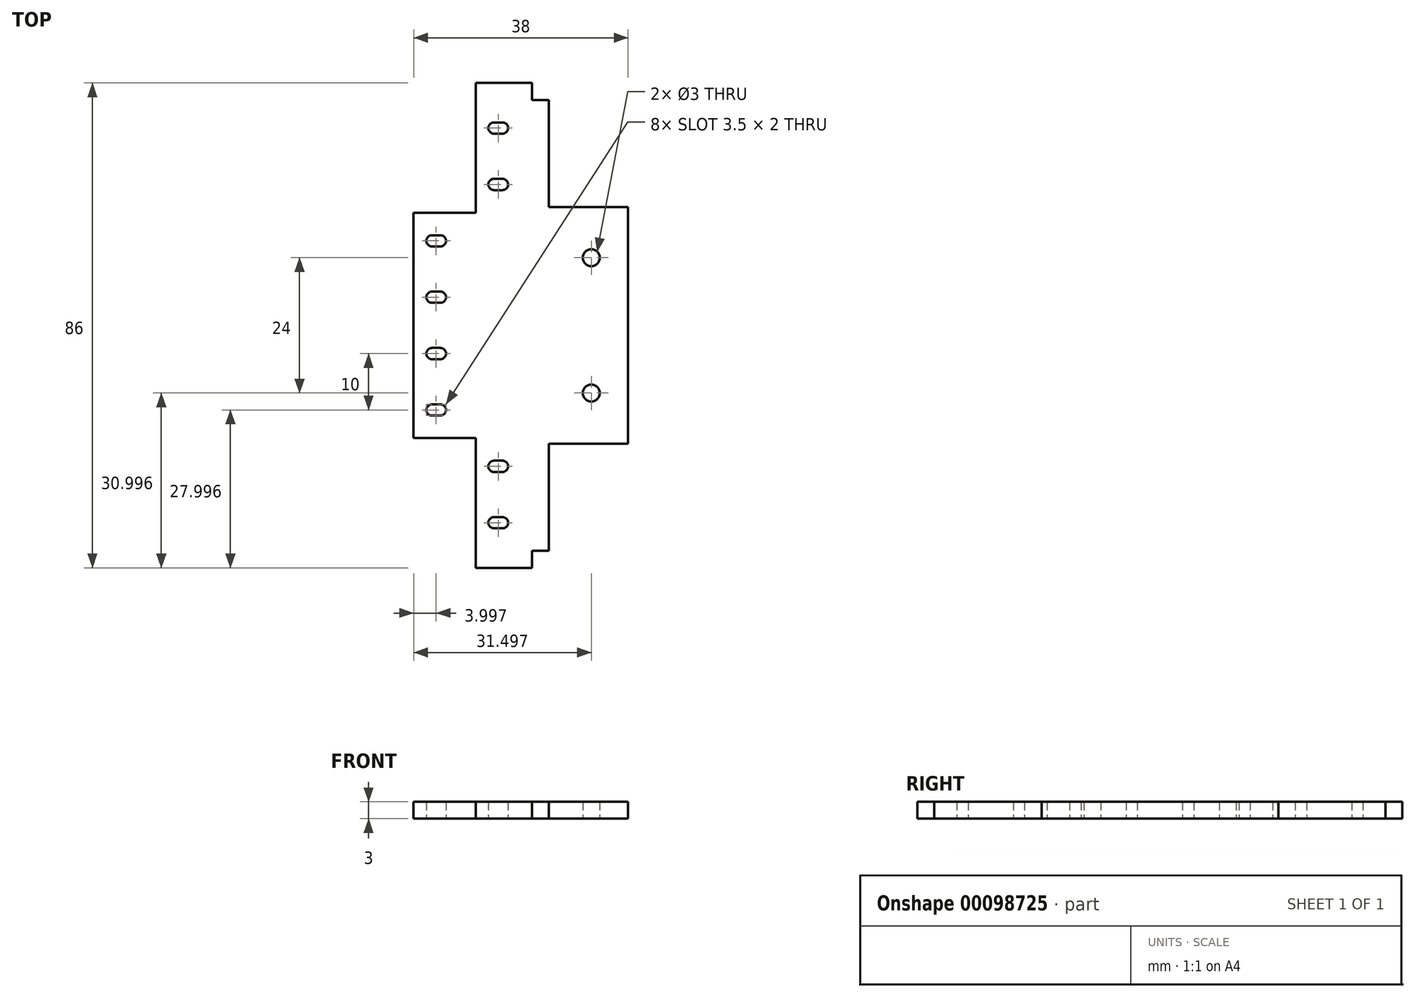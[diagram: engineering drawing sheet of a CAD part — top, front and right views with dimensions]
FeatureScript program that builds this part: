
annotation { "Feature Type Name" : "Feature", "Feature Type Description" : "" }
export const myFeature = defineFeature(function(context is Context, id is Id, definition is map)
    precondition{}
    {
        {
            var Q0;
            Q0=qCreatedBy(makeId("Top.planeOp"),FACE);
            var sketch = newSketch(context, id + "F0", { "sketchPlane" : qUnion([Q0])});
            skLineSegment(sketch, "E0", {"start": v(9.4, 3.28) * mm, "end": v(19.4, 3.28) * mm});
            skLineSegment(sketch, "E1", {"start": v(19.4, 3.28) * mm, "end": v(19.4, 6.28) * mm});
            skLineSegment(sketch, "E2", {"start": v(19.4, 6.28) * mm, "end": v(22.4, 6.28) * mm});
            skLineSegment(sketch, "E3", {"start": v(22.4, 6.28) * mm, "end": v(22.4, 25.28) * mm});
            skLineSegment(sketch, "E4", {"start": v(22.4, 25.28) * mm, "end": v(36.4, 25.28) * mm});
            skLineSegment(sketch, "E5", {"start": v(36.4, 25.28) * mm, "end": v(36.4, 67.28) * mm});
            skLineSegment(sketch, "E6", {"start": v(36.4, 67.28) * mm, "end": v(22.4, 67.28) * mm});
            skLineSegment(sketch, "E7", {"start": v(22.4, 67.28) * mm, "end": v(22.4, 86.28) * mm});
            skLineSegment(sketch, "E8", {"start": v(22.4, 86.28) * mm, "end": v(19.4, 86.28) * mm});
            skLineSegment(sketch, "E9", {"start": v(19.4, 86.28) * mm, "end": v(19.4, 89.28) * mm});
            skLineSegment(sketch, "E10", {"start": v(19.4, 89.28) * mm, "end": v(9.4, 89.28) * mm});
            skLineSegment(sketch, "E11", {"start": v(9.4, 89.28) * mm, "end": v(9.4, 66.28) * mm});
            skLineSegment(sketch, "E12", {"start": v(9.4, 66.28) * mm, "end": v(-1.6, 66.28) * mm});
            skLineSegment(sketch, "E13", {"start": v(-1.6, 66.28) * mm, "end": v(-1.6, 26.28) * mm});
            skLineSegment(sketch, "E14", {"start": v(-1.6, 26.28) * mm, "end": v(9.4, 26.28) * mm});
            skLineSegment(sketch, "E15", {"start": v(9.4, 26.28) * mm, "end": v(9.4, 3.28) * mm});
            skArc(sketch, "E16", {"start": v(0.65, 31.28) * mm, "mid": v(0.94, 30.57) * mm, "end": v(1.65, 30.28) * mm});
            skLineSegment(sketch, "E17", {"start": v(1.65, 30.28) * mm, "end": v(3.15, 30.28) * mm});
            skArc(sketch, "E18", {"start": v(3.15, 30.28) * mm, "mid": v(3.85, 30.57) * mm, "end": v(4.15, 31.28) * mm});
            skArc(sketch, "E19", {"start": v(4.15, 31.28) * mm, "mid": v(3.85, 31.98) * mm, "end": v(3.15, 32.28) * mm});
            skLineSegment(sketch, "E20", {"start": v(3.15, 32.28) * mm, "end": v(1.65, 32.28) * mm});
            skArc(sketch, "E21", {"start": v(1.65, 32.28) * mm, "mid": v(0.94, 31.98) * mm, "end": v(0.65, 31.28) * mm});
            skArc(sketch, "E22", {"start": v(0.65, 41.28) * mm, "mid": v(0.94, 40.57) * mm, "end": v(1.65, 40.28) * mm});
            skLineSegment(sketch, "E23", {"start": v(1.65, 40.28) * mm, "end": v(3.15, 40.28) * mm});
            skArc(sketch, "E24", {"start": v(3.15, 40.28) * mm, "mid": v(3.85, 40.57) * mm, "end": v(4.15, 41.28) * mm});
            skArc(sketch, "E25", {"start": v(4.15, 41.28) * mm, "mid": v(3.85, 41.98) * mm, "end": v(3.15, 42.28) * mm});
            skLineSegment(sketch, "E26", {"start": v(3.15, 42.28) * mm, "end": v(1.65, 42.28) * mm});
            skArc(sketch, "E27", {"start": v(1.65, 42.28) * mm, "mid": v(0.94, 41.98) * mm, "end": v(0.65, 41.28) * mm});
            skArc(sketch, "E28", {"start": v(0.65, 51.28) * mm, "mid": v(0.94, 50.57) * mm, "end": v(1.65, 50.28) * mm});
            skLineSegment(sketch, "E29", {"start": v(1.65, 50.28) * mm, "end": v(3.15, 50.28) * mm});
            skArc(sketch, "E30", {"start": v(3.15, 50.28) * mm, "mid": v(3.85, 50.57) * mm, "end": v(4.15, 51.28) * mm});
            skArc(sketch, "E31", {"start": v(4.15, 51.28) * mm, "mid": v(3.85, 51.98) * mm, "end": v(3.15, 52.28) * mm});
            skLineSegment(sketch, "E32", {"start": v(3.15, 52.28) * mm, "end": v(1.65, 52.28) * mm});
            skArc(sketch, "E33", {"start": v(1.65, 52.28) * mm, "mid": v(0.94, 51.98) * mm, "end": v(0.65, 51.28) * mm});
            skArc(sketch, "E34", {"start": v(0.65, 61.28) * mm, "mid": v(0.94, 60.57) * mm, "end": v(1.65, 60.28) * mm});
            skLineSegment(sketch, "E35", {"start": v(1.65, 60.28) * mm, "end": v(3.15, 60.28) * mm});
            skArc(sketch, "E36", {"start": v(3.15, 60.28) * mm, "mid": v(3.85, 60.57) * mm, "end": v(4.15, 61.28) * mm});
            skArc(sketch, "E37", {"start": v(4.15, 61.28) * mm, "mid": v(3.85, 61.98) * mm, "end": v(3.15, 62.28) * mm});
            skLineSegment(sketch, "E38", {"start": v(3.15, 62.28) * mm, "end": v(1.65, 62.28) * mm});
            skArc(sketch, "E39", {"start": v(1.65, 62.28) * mm, "mid": v(0.94, 61.98) * mm, "end": v(0.65, 61.28) * mm});
            skCircle(sketch, "E40", {"center": v(29.9, 58.28) * mm, "radius": 1.5 * mm});
            skCircle(sketch, "E41", {"center": v(29.9, 34.28) * mm, "radius": 1.5 * mm});
            skArc(sketch, "E42", {"start": v(11.65, 21.28) * mm, "mid": v(11.94, 20.57) * mm, "end": v(12.65, 20.28) * mm});
            skLineSegment(sketch, "E43", {"start": v(12.65, 20.28) * mm, "end": v(14.15, 20.28) * mm});
            skArc(sketch, "E44", {"start": v(14.15, 20.28) * mm, "mid": v(14.85, 20.57) * mm, "end": v(15.15, 21.28) * mm});
            skArc(sketch, "E45", {"start": v(15.15, 21.28) * mm, "mid": v(14.85, 21.98) * mm, "end": v(14.15, 22.28) * mm});
            skLineSegment(sketch, "E46", {"start": v(14.15, 22.28) * mm, "end": v(12.65, 22.28) * mm});
            skArc(sketch, "E47", {"start": v(12.65, 22.28) * mm, "mid": v(11.94, 21.98) * mm, "end": v(11.65, 21.28) * mm});
            skArc(sketch, "E48", {"start": v(11.65, 11.28) * mm, "mid": v(11.94, 10.57) * mm, "end": v(12.65, 10.28) * mm});
            skLineSegment(sketch, "E49", {"start": v(12.65, 10.28) * mm, "end": v(14.15, 10.28) * mm});
            skArc(sketch, "E50", {"start": v(14.15, 10.28) * mm, "mid": v(14.85, 10.57) * mm, "end": v(15.15, 11.28) * mm});
            skArc(sketch, "E51", {"start": v(15.15, 11.28) * mm, "mid": v(14.85, 11.98) * mm, "end": v(14.15, 12.28) * mm});
            skLineSegment(sketch, "E52", {"start": v(14.15, 12.28) * mm, "end": v(12.65, 12.28) * mm});
            skArc(sketch, "E53", {"start": v(12.65, 12.28) * mm, "mid": v(11.94, 11.98) * mm, "end": v(11.65, 11.28) * mm});
            skArc(sketch, "E54", {"start": v(11.65, 81.28) * mm, "mid": v(11.94, 80.57) * mm, "end": v(12.65, 80.28) * mm});
            skLineSegment(sketch, "E55", {"start": v(12.65, 80.28) * mm, "end": v(14.15, 80.28) * mm});
            skArc(sketch, "E56", {"start": v(14.15, 80.28) * mm, "mid": v(14.85, 80.57) * mm, "end": v(15.15, 81.28) * mm});
            skArc(sketch, "E57", {"start": v(15.15, 81.28) * mm, "mid": v(14.85, 81.98) * mm, "end": v(14.15, 82.28) * mm});
            skLineSegment(sketch, "E58", {"start": v(14.15, 82.28) * mm, "end": v(12.65, 82.28) * mm});
            skArc(sketch, "E59", {"start": v(12.65, 82.28) * mm, "mid": v(11.94, 81.98) * mm, "end": v(11.65, 81.28) * mm});
            skArc(sketch, "E60", {"start": v(11.65, 71.28) * mm, "mid": v(11.94, 70.57) * mm, "end": v(12.65, 70.28) * mm});
            skLineSegment(sketch, "E61", {"start": v(12.65, 70.28) * mm, "end": v(14.15, 70.28) * mm});
            skArc(sketch, "E62", {"start": v(14.15, 70.28) * mm, "mid": v(14.85, 70.57) * mm, "end": v(15.15, 71.28) * mm});
            skArc(sketch, "E63", {"start": v(15.15, 71.28) * mm, "mid": v(14.85, 71.98) * mm, "end": v(14.15, 72.28) * mm});
            skLineSegment(sketch, "E64", {"start": v(14.15, 72.28) * mm, "end": v(12.65, 72.28) * mm});
            skArc(sketch, "E65", {"start": v(12.65, 72.28) * mm, "mid": v(11.94, 71.98) * mm, "end": v(11.65, 71.28) * mm});
            skSolve(sketch);
        }
        {
            var Q0;
            Q0=makeQuery(id+"F0.imprint","IMPRINT",FACE,{"disambiguationData":[TD([[makeQuery(id+"F0.imprint","IMPRINT",EDGE,{"derivedFrom":sQuery(id+"F0.wireOp",EDGE,"E0")}),1.0]])]});
            extrude(context, id + "F1", {"entities" : qUnion([Q0]), "depth" : 3 * mm, "symmetric" : true});
        }
    });
